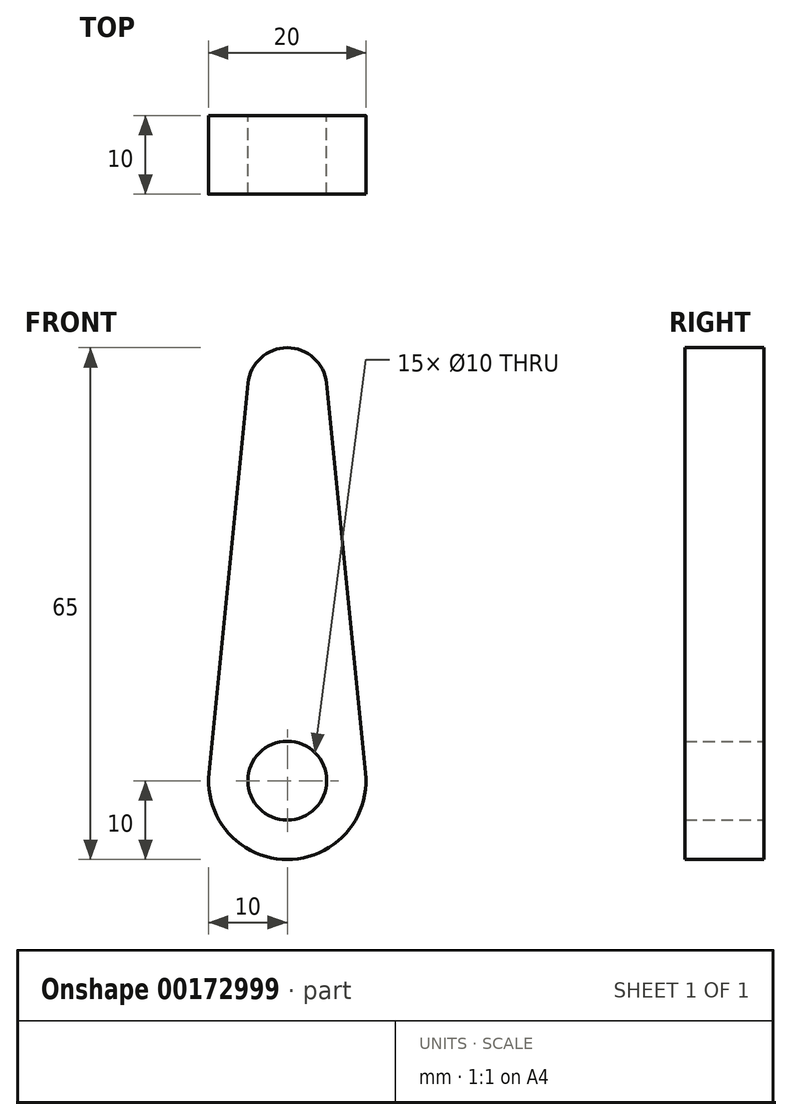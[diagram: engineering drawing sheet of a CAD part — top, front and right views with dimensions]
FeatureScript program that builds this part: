
annotation { "Feature Type Name" : "Feature", "Feature Type Description" : "" }
export const myFeature = defineFeature(function(context is Context, id is Id, definition is map)
    precondition{}
    {
        {
            var Q0;
            Q0=qCreatedBy(makeId("Front.planeOp"),FACE);
            var sketch = newSketch(context, id + "F0", { "sketchPlane" : qUnion([Q0])});
            skCircle(sketch, "E0", {"center": v(0, 0) * mm, "radius": 10 * mm});
            skCircle(sketch, "E1", {"center": v(0, 50) * mm, "radius": 5 * mm});
            skLineSegment(sketch, "E2", {"start": v(-4.97, 50.5) * mm, "end": v(-9.95, 1) * mm});
            skLineSegment(sketch, "E3", {"start": v(0, 50) * mm, "end": v(0, 0) * mm, "construction": true});
            skLineSegment(sketch, "E4.MirrorCS", {"start": v(4.97, 50.5) * mm, "end": v(9.95, 1) * mm});
            skSolve(sketch);
        }
        {
            var Q0;
            Q0=qSketchRegion(id+"F0",true);
            extrude(context, id + "F1", {"entities" : qUnion([Q0]), "depth" : 10 * mm});
        }
        {
            var Q0;
            Q0=makeQuery(id+"F1.opExtrude","CAP_FACE",FACE,{"disambiguationData":[OSD([sQuery(id+"F0.wireOp",EDGE,"E0"),sQuery(id+"F0.wireOp",EDGE,"E1"),sQuery(id+"F0.wireOp",EDGE,"E2"),sQuery(id+"F0.wireOp",EDGE,"E4.MirrorCS")])],"isStart":true});
            var sketch = newSketch(context, id + "F2", { "sketchPlane" : qUnion([Q0])});
            skCircle(sketch, "E5", {"center": v(0, 0) * mm, "radius": 5 * mm});
            skSolve(sketch);
        }
        {
            var Q0;
            Q0=qSketchRegion(id+"F2",true);
            extrude(context, id + "F3", {"entities" : qUnion([Q0]), "operationType" : NewBodyOperationType.REMOVE, "oppositeDirection" : true, "depth" : 10 * mm});
        }
    });
